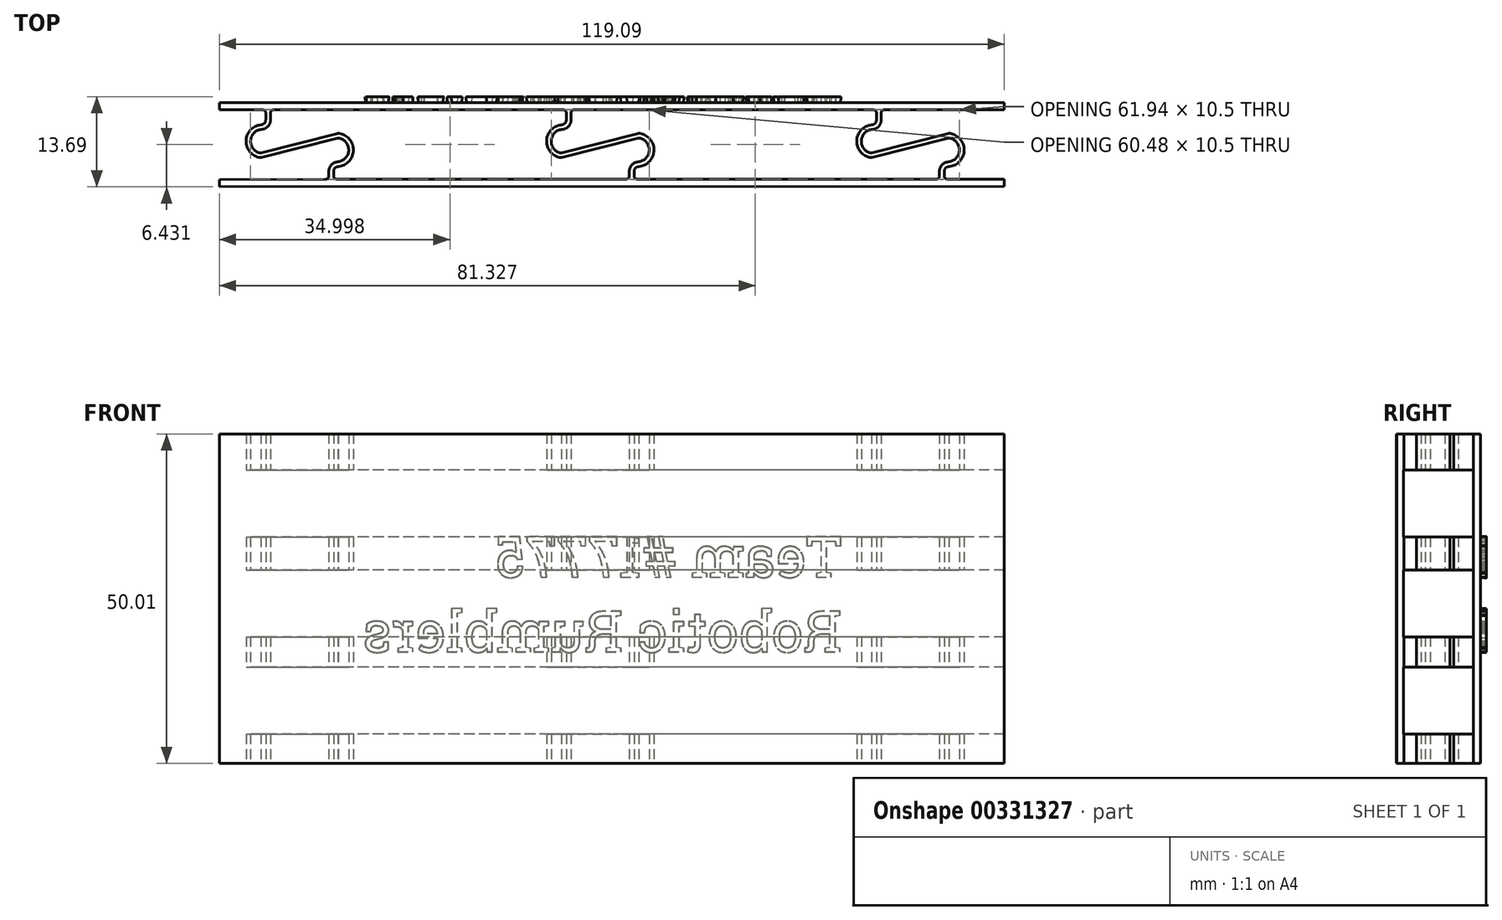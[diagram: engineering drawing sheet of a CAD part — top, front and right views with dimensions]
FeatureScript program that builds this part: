
annotation { "Feature Type Name" : "Feature", "Feature Type Description" : "" }
export const myFeature = defineFeature(function(context is Context, id is Id, definition is map)
    precondition{}
    {
        {
            var Q0;
            Q0=qCreatedBy(makeId("Top.planeOp"),FACE);
            var sketch = newSketch(context, id + "F0", { "sketchPlane" : qUnion([Q0])});
            skLineSegment(sketch, "E0", {"start": v(159.96, 0.09) * mm, "end": v(159.96, -1.43) * mm});
            skLineSegment(sketch, "E1", {"start": v(160.97, 0.09) * mm, "end": v(160.97, -1.43) * mm});
            skArc(sketch, "E2", {"start": v(160.97, -1.43) * mm, "mid": v(160.38, -2.87) * mm, "end": v(158.93, -3.46) * mm});
            skArc(sketch, "E3", {"start": v(159.96, -1.43) * mm, "mid": v(159.67, -2.16) * mm, "end": v(158.95, -2.48) * mm});
            skArc(sketch, "E4", {"start": v(158.93, -3.46) * mm, "mid": v(156.76, -5.9) * mm, "end": v(158.8, -8.45) * mm});
            skArc(sketch, "E5", {"start": v(158.95, -2.48) * mm, "mid": v(155.8, -5.9) * mm, "end": v(158.81, -9.43) * mm});
            skLineSegment(sketch, "E6", {"start": v(174.33, -13.38) * mm, "end": v(174.33, -12.37) * mm});
            skLineSegment(sketch, "E7", {"start": v(173.31, -13.38) * mm, "end": v(173.31, -12.37) * mm});
            skArc(sketch, "E8", {"start": v(173.31, -12.37) * mm, "mid": v(173.9, -10.94) * mm, "end": v(175.3, -10.32) * mm});
            skArc(sketch, "E9", {"start": v(174.33, -12.37) * mm, "mid": v(174.63, -11.63) * mm, "end": v(175.37, -11.32) * mm});
            skArc(sketch, "E10", {"start": v(175.3, -10.32) * mm, "mid": v(177.55, -7.87) * mm, "end": v(175.43, -5.3) * mm});
            skArc(sketch, "E11", {"start": v(175.37, -11.32) * mm, "mid": v(178.55, -7.83) * mm, "end": v(175.4, -4.29) * mm});
            skLineSegment(sketch, "E12", {"start": v(159.04, -9.42) * mm, "end": v(175.18, -5.32) * mm});
            skLineSegment(sketch, "E13", {"start": v(175.2, -4.3) * mm, "end": v(159.06, -8.44) * mm});
            skPoint(sketch, "E14.visualSharp", {"position": v(158.93, -8.47) * mm});
            skArc(sketch, "E14.filletArc", {"start": v(158.8, -8.45) * mm, "mid": v(158.92, -8.46) * mm, "end": v(159.06, -8.44) * mm});
            skPoint(sketch, "E15.visualSharp", {"position": v(158.93, -9.45) * mm});
            skArc(sketch, "E15.filletArc", {"start": v(158.81, -9.43) * mm, "mid": v(158.93, -9.44) * mm, "end": v(159.04, -9.42) * mm});
            skPoint(sketch, "E16.visualSharp", {"position": v(175.3, -4.28) * mm});
            skArc(sketch, "E16.filletArc", {"start": v(175.4, -4.29) * mm, "mid": v(175.3, -4.29) * mm, "end": v(175.2, -4.3) * mm});
            skPoint(sketch, "E17.visualSharp", {"position": v(175.3, -5.29) * mm});
            skArc(sketch, "E17.filletArc", {"start": v(175.43, -5.3) * mm, "mid": v(175.3, -5.3) * mm, "end": v(175.18, -5.32) * mm});
            skLineSegment(sketch, "E18", {"start": v(44.92, -13.98) * mm, "end": v(172.72, -13.98) * mm});
            skLineSegment(sketch, "E19", {"start": v(161.57, 0.68) * mm, "end": v(187.04, 0.68) * mm});
            skLineSegment(sketch, "E20", {"start": v(187.04, 0.68) * mm, "end": v(187.04, 2.22) * mm});
            skLineSegment(sketch, "E21", {"start": v(174.93, -13.98) * mm, "end": v(187.04, -13.98) * mm});
            skLineSegment(sketch, "E22", {"start": v(187.04, -13.98) * mm, "end": v(187.04, -15.5) * mm});
            skPoint(sketch, "E23.visualSharp", {"position": v(160.97, 0.68) * mm});
            skArc(sketch, "E23.filletArc", {"start": v(161.57, 0.68) * mm, "mid": v(161.15, 0.5) * mm, "end": v(160.97, 0.09) * mm});
            skPoint(sketch, "E24.visualSharp", {"position": v(159.96, 0.68) * mm});
            skArc(sketch, "E24.filletArc", {"start": v(159.96, 0.09) * mm, "mid": v(159.78, 0.5) * mm, "end": v(159.36, 0.68) * mm});
            skPoint(sketch, "E25.visualSharp", {"position": v(174.33, -13.98) * mm});
            skArc(sketch, "E25.filletArc", {"start": v(174.33, -13.38) * mm, "mid": v(174.5, -13.8) * mm, "end": v(174.93, -13.98) * mm});
            skPoint(sketch, "E26.visualSharp", {"position": v(173.31, -13.98) * mm});
            skArc(sketch, "E26.filletArc", {"start": v(172.72, -13.98) * mm, "mid": v(173.14, -13.8) * mm, "end": v(173.31, -13.38) * mm});
            skLineSegment(sketch, "E27", {"start": v(31.57, 0.09) * mm, "end": v(31.57, -1.43) * mm});
            skArc(sketch, "E28", {"start": v(31.57, -1.43) * mm, "mid": v(30.97, -2.87) * mm, "end": v(29.52, -3.46) * mm});
            skArc(sketch, "E29", {"start": v(30.55, -1.43) * mm, "mid": v(30.26, -2.16) * mm, "end": v(29.54, -2.48) * mm});
            skArc(sketch, "E30", {"start": v(29.52, -3.46) * mm, "mid": v(27.35, -5.9) * mm, "end": v(29.38, -8.45) * mm});
            skArc(sketch, "E31", {"start": v(29.54, -2.48) * mm, "mid": v(26.38, -5.9) * mm, "end": v(29.4, -9.43) * mm});
            skLineSegment(sketch, "E32", {"start": v(44.92, -13.38) * mm, "end": v(44.92, -12.37) * mm});
            skLineSegment(sketch, "E33", {"start": v(43.9, -13.38) * mm, "end": v(43.9, -12.37) * mm});
            skArc(sketch, "E34", {"start": v(43.9, -12.37) * mm, "mid": v(44.48, -10.94) * mm, "end": v(45.89, -10.32) * mm});
            skArc(sketch, "E35", {"start": v(44.92, -12.37) * mm, "mid": v(45.22, -11.63) * mm, "end": v(45.96, -11.32) * mm});
            skArc(sketch, "E36", {"start": v(45.89, -10.32) * mm, "mid": v(48.14, -7.87) * mm, "end": v(46.02, -5.3) * mm});
            skArc(sketch, "E37", {"start": v(45.96, -11.32) * mm, "mid": v(49.14, -7.83) * mm, "end": v(46, -4.29) * mm});
            skLineSegment(sketch, "E38", {"start": v(29.63, -9.42) * mm, "end": v(45.77, -5.32) * mm});
            skLineSegment(sketch, "E39", {"start": v(45.78, -4.3) * mm, "end": v(29.65, -8.44) * mm});
            skPoint(sketch, "E40.visualSharp", {"position": v(29.52, -8.47) * mm});
            skArc(sketch, "E40.filletArc", {"start": v(29.38, -8.45) * mm, "mid": v(29.52, -8.46) * mm, "end": v(29.65, -8.44) * mm});
            skPoint(sketch, "E41.visualSharp", {"position": v(29.52, -9.45) * mm});
            skArc(sketch, "E41.filletArc", {"start": v(29.4, -9.43) * mm, "mid": v(29.52, -9.44) * mm, "end": v(29.63, -9.42) * mm});
            skPoint(sketch, "E42.visualSharp", {"position": v(45.89, -4.28) * mm});
            skArc(sketch, "E42.filletArc", {"start": v(46, -4.29) * mm, "mid": v(45.9, -4.29) * mm, "end": v(45.78, -4.3) * mm});
            skPoint(sketch, "E43.visualSharp", {"position": v(45.89, -5.29) * mm});
            skArc(sketch, "E43.filletArc", {"start": v(46.02, -5.3) * mm, "mid": v(45.9, -5.3) * mm, "end": v(45.77, -5.32) * mm});
            skPoint(sketch, "E44.visualSharp", {"position": v(31.57, 0) * mm});
            skArc(sketch, "E44.filletArc", {"start": v(32.16, 0.68) * mm, "mid": v(31.74, 0.5) * mm, "end": v(31.57, 0.09) * mm});
            skPoint(sketch, "E45.visualSharp", {"position": v(44.92, -13.98) * mm});
            skArc(sketch, "E45.filletArc", {"start": v(44.92, -13.38) * mm, "mid": v(45.1, -13.8) * mm, "end": v(45.52, -13.98) * mm});
            skPoint(sketch, "E46.visualSharp", {"position": v(43.9, -13.98) * mm});
            skArc(sketch, "E46.filletArc", {"start": v(43.31, -13.98) * mm, "mid": v(43.73, -13.8) * mm, "end": v(43.9, -13.38) * mm});
            skLineSegment(sketch, "E47", {"start": v(187.04, 2.22) * mm, "end": v(20.7, 2.22) * mm});
            skLineSegment(sketch, "E48", {"start": v(43.31, -13.98) * mm, "end": v(20.7, -14.1) * mm});
            skLineSegment(sketch, "E49", {"start": v(20.7, -14.1) * mm, "end": v(20.71, -15.63) * mm});
            skLineSegment(sketch, "E50", {"start": v(20.71, -15.63) * mm, "end": v(187.04, -15.5) * mm});
            skLineSegment(sketch, "E51", {"start": v(20.7, 2.22) * mm, "end": v(20.7, 0.7) * mm});
            skLineSegment(sketch, "E52", {"start": v(30.55, -1.43) * mm, "end": v(30.55, 0.1) * mm});
            skLineSegment(sketch, "E53", {"start": v(29.95, 0.7) * mm, "end": v(20.7, 0.7) * mm});
            skPoint(sketch, "E54.visualSharp", {"position": v(30.55, 0.7) * mm});
            skArc(sketch, "E54.filletArc", {"start": v(30.55, 0.1) * mm, "mid": v(30.38, 0.52) * mm, "end": v(29.95, 0.7) * mm});
            skLineSegment(sketch, "E55", {"start": v(94.24, 0.09) * mm, "end": v(94.24, -1.43) * mm});
            skLineSegment(sketch, "E56", {"start": v(95.25, 0.09) * mm, "end": v(95.25, -1.43) * mm});
            skArc(sketch, "E57", {"start": v(95.25, -1.43) * mm, "mid": v(94.66, -2.87) * mm, "end": v(93.21, -3.46) * mm});
            skArc(sketch, "E58", {"start": v(94.24, -1.43) * mm, "mid": v(93.94, -2.16) * mm, "end": v(93.23, -2.48) * mm});
            skArc(sketch, "E59", {"start": v(93.21, -3.46) * mm, "mid": v(91.04, -5.9) * mm, "end": v(93.07, -8.45) * mm});
            skArc(sketch, "E60", {"start": v(93.23, -2.48) * mm, "mid": v(90.07, -5.9) * mm, "end": v(93.1, -9.43) * mm});
            skLineSegment(sketch, "E61", {"start": v(108.61, -13.38) * mm, "end": v(108.61, -12.37) * mm});
            skLineSegment(sketch, "E62", {"start": v(107.6, -13.38) * mm, "end": v(107.6, -12.37) * mm});
            skArc(sketch, "E63", {"start": v(107.6, -12.37) * mm, "mid": v(108.17, -10.94) * mm, "end": v(109.57, -10.32) * mm});
            skArc(sketch, "E64", {"start": v(108.61, -12.37) * mm, "mid": v(108.91, -11.63) * mm, "end": v(109.64, -11.32) * mm});
            skArc(sketch, "E65", {"start": v(109.57, -10.32) * mm, "mid": v(111.83, -7.87) * mm, "end": v(109.7, -5.3) * mm});
            skArc(sketch, "E66", {"start": v(109.64, -11.32) * mm, "mid": v(112.83, -7.83) * mm, "end": v(109.69, -4.29) * mm});
            skLineSegment(sketch, "E67", {"start": v(93.32, -9.42) * mm, "end": v(109.46, -5.32) * mm});
            skLineSegment(sketch, "E68", {"start": v(109.47, -4.3) * mm, "end": v(93.34, -8.44) * mm});
            skPoint(sketch, "E69.visualSharp", {"position": v(93.21, -8.47) * mm});
            skArc(sketch, "E69.filletArc", {"start": v(93.07, -8.45) * mm, "mid": v(93.2, -8.46) * mm, "end": v(93.34, -8.44) * mm});
            skPoint(sketch, "E70.visualSharp", {"position": v(93.21, -9.45) * mm});
            skArc(sketch, "E70.filletArc", {"start": v(93.1, -9.43) * mm, "mid": v(93.2, -9.44) * mm, "end": v(93.32, -9.42) * mm});
            skPoint(sketch, "E71.visualSharp", {"position": v(109.57, -4.28) * mm});
            skArc(sketch, "E71.filletArc", {"start": v(109.69, -4.29) * mm, "mid": v(109.58, -4.29) * mm, "end": v(109.47, -4.3) * mm});
            skPoint(sketch, "E72.visualSharp", {"position": v(109.57, -5.29) * mm});
            skArc(sketch, "E72.filletArc", {"start": v(109.7, -5.3) * mm, "mid": v(109.58, -5.3) * mm, "end": v(109.46, -5.32) * mm});
            skPoint(sketch, "E73.visualSharp", {"position": v(95.25, 0.68) * mm});
            skArc(sketch, "E73.filletArc", {"start": v(95.85, 0.68) * mm, "mid": v(95.43, 0.5) * mm, "end": v(95.25, 0.09) * mm});
            skPoint(sketch, "E74.visualSharp", {"position": v(94.24, 0.68) * mm});
            skArc(sketch, "E74.filletArc", {"start": v(94.24, 0.09) * mm, "mid": v(94.06, 0.5) * mm, "end": v(93.64, 0.68) * mm});
            skPoint(sketch, "E75.visualSharp", {"position": v(108.61, -13.98) * mm});
            skArc(sketch, "E75.filletArc", {"start": v(108.61, -13.38) * mm, "mid": v(108.79, -13.8) * mm, "end": v(109.2, -13.98) * mm});
            skPoint(sketch, "E76.visualSharp", {"position": v(107.6, -13.98) * mm});
            skArc(sketch, "E76.filletArc", {"start": v(107, -13.98) * mm, "mid": v(107.42, -13.8) * mm, "end": v(107.6, -13.38) * mm});
            skLineSegment(sketch, "E77", {"start": v(32.16, 0.68) * mm, "end": v(93.64, 0.68) * mm});
            skLineSegment(sketch, "E78", {"start": v(95.85, 0.68) * mm, "end": v(159.36, 0.68) * mm});
            skSolve(sketch);
        }
        {
            var Q0;
            Q0=makeQuery(id+"F0.imprint","IMPRINT",FACE,{"disambiguationData":[TD([[makeQuery(id+"F0.imprint","IMPRINT",EDGE,{"derivedFrom":sQuery(id+"F0.wireOp",EDGE,"E0")}),1.0]])]});
            extrude(context, id + "F1", {"entities" : qUnion([Q0]), "depth" : 69.85 * mm});
        }
        {
            var Q0;
            Q0=makeQuery(id+"F1.opExtrude","SWEPT_FACE",FACE,{"disambiguationData":[OSD([sQuery(id+"F0.wireOp",EDGE,"E51")])]});
            var sketch = newSketch(context, id + "F2", { "sketchPlane" : qUnion([Q0])});
            skLineSegment(sketch, "E79.bottom", {"start": v(-0.7, 6.25) * mm, "end": v(14.06, 6.25) * mm});
            skLineSegment(sketch, "E79.top", {"start": v(-0.7, 20.44) * mm, "end": v(14.06, 20.44) * mm});
            skLineSegment(sketch, "E79.left", {"start": v(-0.7, 6.25) * mm, "end": v(-0.7, 20.44) * mm});
            skLineSegment(sketch, "E79.right", {"start": v(14.06, 6.25) * mm, "end": v(14.06, 20.44) * mm});
            skLineSegment(sketch, "E80.bottom", {"start": v(-0.7, 26.84) * mm, "end": v(14.06, 26.84) * mm});
            skLineSegment(sketch, "E80.top", {"start": v(-0.7, 41.03) * mm, "end": v(14.06, 41.03) * mm});
            skLineSegment(sketch, "E80.left", {"start": v(-0.7, 26.84) * mm, "end": v(-0.7, 41.03) * mm});
            skLineSegment(sketch, "E80.right", {"start": v(14.06, 26.84) * mm, "end": v(14.06, 41.03) * mm});
            skLineSegment(sketch, "E81.bottom", {"start": v(-0.7, 48.02) * mm, "end": v(14.06, 48.02) * mm});
            skLineSegment(sketch, "E81.top", {"start": v(-0.7, 62.2) * mm, "end": v(14.06, 62.2) * mm});
            skLineSegment(sketch, "E81.left", {"start": v(-0.7, 48.02) * mm, "end": v(-0.7, 62.2) * mm});
            skLineSegment(sketch, "E81.right", {"start": v(14.06, 48.02) * mm, "end": v(14.06, 62.2) * mm});
            skSolve(sketch);
        }
        {
            var Q0;
            Q0=makeQuery(id+"F2.imprint","IMPRINT",FACE,{"disambiguationData":[TD([[makeQuery(id+"F2.imprint","IMPRINT",EDGE,{"derivedFrom":sQuery(id+"F2.wireOp",EDGE,"E79.bottom")}),1.0]])]});
            var Q1;
            Q1=makeQuery(id+"F2.imprint","IMPRINT",FACE,{"disambiguationData":[TD([[makeQuery(id+"F2.imprint","IMPRINT",EDGE,{"derivedFrom":sQuery(id+"F2.wireOp",EDGE,"E80.bottom")}),1.0]])]});
            var Q2;
            Q2=makeQuery(id+"F2.imprint","IMPRINT",FACE,{"disambiguationData":[TD([[makeQuery(id+"F2.imprint","IMPRINT",EDGE,{"derivedFrom":sQuery(id+"F2.wireOp",EDGE,"E81.bottom")}),1.0]])]});
            extrude(context, id + "F3", {"entities" : qUnion([Q0, Q1, Q2]), "operationType" : NewBodyOperationType.REMOVE, "oppositeDirection" : true, "depth" : 254 * mm});
        }
        {
            var Q0;
            Q0=makeQuery(id+"F1.opExtrude","SWEPT_FACE",FACE,{"disambiguationData":[OSD([sQuery(id+"F0.wireOp",EDGE,"E47")])]});
            var sketch = newSketch(context, id + "F4", { "sketchPlane" : qUnion([Q0])});
            skText(sketch, "E82", { "text": "Team #17775\nRobotic Rumblers", "fontName": "RobotoSlab-Regular.ttf"});
            const initialGuessF4  = {"E82": [-0.15258, 0.03953, 1, 0, 0.00865]};
            skSetInitialGuess(sketch, initialGuessF4);
            skSolve(sketch);
        }
        {
            var Q0;
            Q0 = qSketchRegion(id + "F4", true);
            extrude(context, id + "F5", {"entities" : qUnion([Q0]), "operationType" : NewBodyOperationType.ADD, "depth" : 1.27 * mm, "hasDraft" : true, "draftAngle" : 3 * degree});
        }
        {
            var Q0;
            Q0=makeQuery(id+"F1.opExtrude","SWEPT_BODY",BODY,{"disambiguationData":[OSD([sQuery(id+"F0.wireOp",EDGE,"E0"),sQuery(id+"F0.wireOp",EDGE,"E1"),sQuery(id+"F0.wireOp",EDGE,"E2"),sQuery(id+"F0.wireOp",EDGE,"E3"),sQuery(id+"F0.wireOp",EDGE,"E4"),sQuery(id+"F0.wireOp",EDGE,"E5"),sQuery(id+"F0.wireOp",EDGE,"E6"),sQuery(id+"F0.wireOp",EDGE,"E7"),sQuery(id+"F0.wireOp",EDGE,"E8"),sQuery(id+"F0.wireOp",EDGE,"E9"),sQuery(id+"F0.wireOp",EDGE,"E10"),sQuery(id+"F0.wireOp",EDGE,"E11"),sQuery(id+"F0.wireOp",EDGE,"E12"),sQuery(id+"F0.wireOp",EDGE,"E13"),sQuery(id+"F0.wireOp",EDGE,"E14.filletArc"),sQuery(id+"F0.wireOp",EDGE,"E15.filletArc"),sQuery(id+"F0.wireOp",EDGE,"E16.filletArc"),sQuery(id+"F0.wireOp",EDGE,"E17.filletArc"),sQuery(id+"F0.wireOp",EDGE,"E18"),sQuery(id+"F0.wireOp",EDGE,"E19"),sQuery(id+"F0.wireOp",EDGE,"E20"),sQuery(id+"F0.wireOp",EDGE,"E21"),sQuery(id+"F0.wireOp",EDGE,"E22"),sQuery(id+"F0.wireOp",EDGE,"E23.filletArc"),sQuery(id+"F0.wireOp",EDGE,"E24.filletArc"),sQuery(id+"F0.wireOp",EDGE,"E25.filletArc"),sQuery(id+"F0.wireOp",EDGE,"E26.filletArc"),sQuery(id+"F0.wireOp",EDGE,"E27"),sQuery(id+"F0.wireOp",EDGE,"E28"),sQuery(id+"F0.wireOp",EDGE,"E29"),sQuery(id+"F0.wireOp",EDGE,"E30"),sQuery(id+"F0.wireOp",EDGE,"E31"),sQuery(id+"F0.wireOp",EDGE,"E32"),sQuery(id+"F0.wireOp",EDGE,"E33"),sQuery(id+"F0.wireOp",EDGE,"E34"),sQuery(id+"F0.wireOp",EDGE,"E35"),sQuery(id+"F0.wireOp",EDGE,"E36"),sQuery(id+"F0.wireOp",EDGE,"E37"),sQuery(id+"F0.wireOp",EDGE,"E38"),sQuery(id+"F0.wireOp",EDGE,"E39"),sQuery(id+"F0.wireOp",EDGE,"E40.filletArc"),sQuery(id+"F0.wireOp",EDGE,"E41.filletArc"),sQuery(id+"F0.wireOp",EDGE,"E42.filletArc"),sQuery(id+"F0.wireOp",EDGE,"E43.filletArc"),sQuery(id+"F0.wireOp",EDGE,"E44.filletArc"),sQuery(id+"F0.wireOp",EDGE,"E45.filletArc"),sQuery(id+"F0.wireOp",EDGE,"E46.filletArc"),sQuery(id+"F0.wireOp",EDGE,"E47"),sQuery(id+"F0.wireOp",EDGE,"E48"),sQuery(id+"F0.wireOp",EDGE,"E49"),sQuery(id+"F0.wireOp",EDGE,"E50"),sQuery(id+"F0.wireOp",EDGE,"E51"),sQuery(id+"F0.wireOp",EDGE,"E52"),sQuery(id+"F0.wireOp",EDGE,"E53"),sQuery(id+"F0.wireOp",EDGE,"E54.filletArc"),sQuery(id+"F0.wireOp",EDGE,"E55"),sQuery(id+"F0.wireOp",EDGE,"E56"),sQuery(id+"F0.wireOp",EDGE,"E57"),sQuery(id+"F0.wireOp",EDGE,"E58"),sQuery(id+"F0.wireOp",EDGE,"E59"),sQuery(id+"F0.wireOp",EDGE,"E60"),sQuery(id+"F0.wireOp",EDGE,"E61"),sQuery(id+"F0.wireOp",EDGE,"E62"),sQuery(id+"F0.wireOp",EDGE,"E63"),sQuery(id+"F0.wireOp",EDGE,"E64"),sQuery(id+"F0.wireOp",EDGE,"E65"),sQuery(id+"F0.wireOp",EDGE,"E66"),sQuery(id+"F0.wireOp",EDGE,"E67"),sQuery(id+"F0.wireOp",EDGE,"E68"),sQuery(id+"F0.wireOp",EDGE,"E69.filletArc"),sQuery(id+"F0.wireOp",EDGE,"E70.filletArc"),sQuery(id+"F0.wireOp",EDGE,"E71.filletArc"),sQuery(id+"F0.wireOp",EDGE,"E72.filletArc"),sQuery(id+"F0.wireOp",EDGE,"E73.filletArc"),sQuery(id+"F0.wireOp",EDGE,"E74.filletArc"),sQuery(id+"F0.wireOp",EDGE,"E75.filletArc"),sQuery(id+"F0.wireOp",EDGE,"E76.filletArc"),sQuery(id+"F0.wireOp",EDGE,"E77"),sQuery(id+"F0.wireOp",EDGE,"E78")])]});
            transform(context, id + "F6", {"entities" : qUnion([Q0]), "transformType" : TransformType.TRANSLATION_3D, "dx" : -104.65 * mm, "dy" : 0 * mm, "dz" : 0 * mm, "makeCopy" : false});
        }
        {
            var Q0;
            Q0=makeQuery(id+"F1.opExtrude","SWEPT_BODY",BODY,{"disambiguationData":[OSD([sQuery(id+"F0.wireOp",EDGE,"E0"),sQuery(id+"F0.wireOp",EDGE,"E1"),sQuery(id+"F0.wireOp",EDGE,"E2"),sQuery(id+"F0.wireOp",EDGE,"E3"),sQuery(id+"F0.wireOp",EDGE,"E4"),sQuery(id+"F0.wireOp",EDGE,"E5"),sQuery(id+"F0.wireOp",EDGE,"E6"),sQuery(id+"F0.wireOp",EDGE,"E7"),sQuery(id+"F0.wireOp",EDGE,"E8"),sQuery(id+"F0.wireOp",EDGE,"E9"),sQuery(id+"F0.wireOp",EDGE,"E10"),sQuery(id+"F0.wireOp",EDGE,"E11"),sQuery(id+"F0.wireOp",EDGE,"E12"),sQuery(id+"F0.wireOp",EDGE,"E13"),sQuery(id+"F0.wireOp",EDGE,"E14.filletArc"),sQuery(id+"F0.wireOp",EDGE,"E15.filletArc"),sQuery(id+"F0.wireOp",EDGE,"E16.filletArc"),sQuery(id+"F0.wireOp",EDGE,"E17.filletArc"),sQuery(id+"F0.wireOp",EDGE,"E18"),sQuery(id+"F0.wireOp",EDGE,"E19"),sQuery(id+"F0.wireOp",EDGE,"E20"),sQuery(id+"F0.wireOp",EDGE,"E21"),sQuery(id+"F0.wireOp",EDGE,"E22"),sQuery(id+"F0.wireOp",EDGE,"E23.filletArc"),sQuery(id+"F0.wireOp",EDGE,"E24.filletArc"),sQuery(id+"F0.wireOp",EDGE,"E25.filletArc"),sQuery(id+"F0.wireOp",EDGE,"E26.filletArc"),sQuery(id+"F0.wireOp",EDGE,"E27"),sQuery(id+"F0.wireOp",EDGE,"E28"),sQuery(id+"F0.wireOp",EDGE,"E29"),sQuery(id+"F0.wireOp",EDGE,"E30"),sQuery(id+"F0.wireOp",EDGE,"E31"),sQuery(id+"F0.wireOp",EDGE,"E32"),sQuery(id+"F0.wireOp",EDGE,"E33"),sQuery(id+"F0.wireOp",EDGE,"E34"),sQuery(id+"F0.wireOp",EDGE,"E35"),sQuery(id+"F0.wireOp",EDGE,"E36"),sQuery(id+"F0.wireOp",EDGE,"E37"),sQuery(id+"F0.wireOp",EDGE,"E38"),sQuery(id+"F0.wireOp",EDGE,"E39"),sQuery(id+"F0.wireOp",EDGE,"E40.filletArc"),sQuery(id+"F0.wireOp",EDGE,"E41.filletArc"),sQuery(id+"F0.wireOp",EDGE,"E42.filletArc"),sQuery(id+"F0.wireOp",EDGE,"E43.filletArc"),sQuery(id+"F0.wireOp",EDGE,"E44.filletArc"),sQuery(id+"F0.wireOp",EDGE,"E45.filletArc"),sQuery(id+"F0.wireOp",EDGE,"E46.filletArc"),sQuery(id+"F0.wireOp",EDGE,"E47"),sQuery(id+"F0.wireOp",EDGE,"E48"),sQuery(id+"F0.wireOp",EDGE,"E49"),sQuery(id+"F0.wireOp",EDGE,"E50"),sQuery(id+"F0.wireOp",EDGE,"E51"),sQuery(id+"F0.wireOp",EDGE,"E52"),sQuery(id+"F0.wireOp",EDGE,"E53"),sQuery(id+"F0.wireOp",EDGE,"E54.filletArc"),sQuery(id+"F0.wireOp",EDGE,"E55"),sQuery(id+"F0.wireOp",EDGE,"E56"),sQuery(id+"F0.wireOp",EDGE,"E57"),sQuery(id+"F0.wireOp",EDGE,"E58"),sQuery(id+"F0.wireOp",EDGE,"E59"),sQuery(id+"F0.wireOp",EDGE,"E60"),sQuery(id+"F0.wireOp",EDGE,"E61"),sQuery(id+"F0.wireOp",EDGE,"E62"),sQuery(id+"F0.wireOp",EDGE,"E63"),sQuery(id+"F0.wireOp",EDGE,"E64"),sQuery(id+"F0.wireOp",EDGE,"E65"),sQuery(id+"F0.wireOp",EDGE,"E66"),sQuery(id+"F0.wireOp",EDGE,"E67"),sQuery(id+"F0.wireOp",EDGE,"E68"),sQuery(id+"F0.wireOp",EDGE,"E69.filletArc"),sQuery(id+"F0.wireOp",EDGE,"E70.filletArc"),sQuery(id+"F0.wireOp",EDGE,"E71.filletArc"),sQuery(id+"F0.wireOp",EDGE,"E72.filletArc"),sQuery(id+"F0.wireOp",EDGE,"E73.filletArc"),sQuery(id+"F0.wireOp",EDGE,"E74.filletArc"),sQuery(id+"F0.wireOp",EDGE,"E75.filletArc"),sQuery(id+"F0.wireOp",EDGE,"E76.filletArc"),sQuery(id+"F0.wireOp",EDGE,"E77"),sQuery(id+"F0.wireOp",EDGE,"E78")])]});
            var Q1;
            Q1=qCreatedBy(makeId("Origin.pointOp"),VERTEX);
            transform(context, id + "F7", {"entities" : qUnion([Q0]), "transformType" : TransformType.SCALE_UNIFORMLY, "scale" : .716, "scalePoint" : qUnion([Q1]), "makeCopy" : false});
        }
    });
